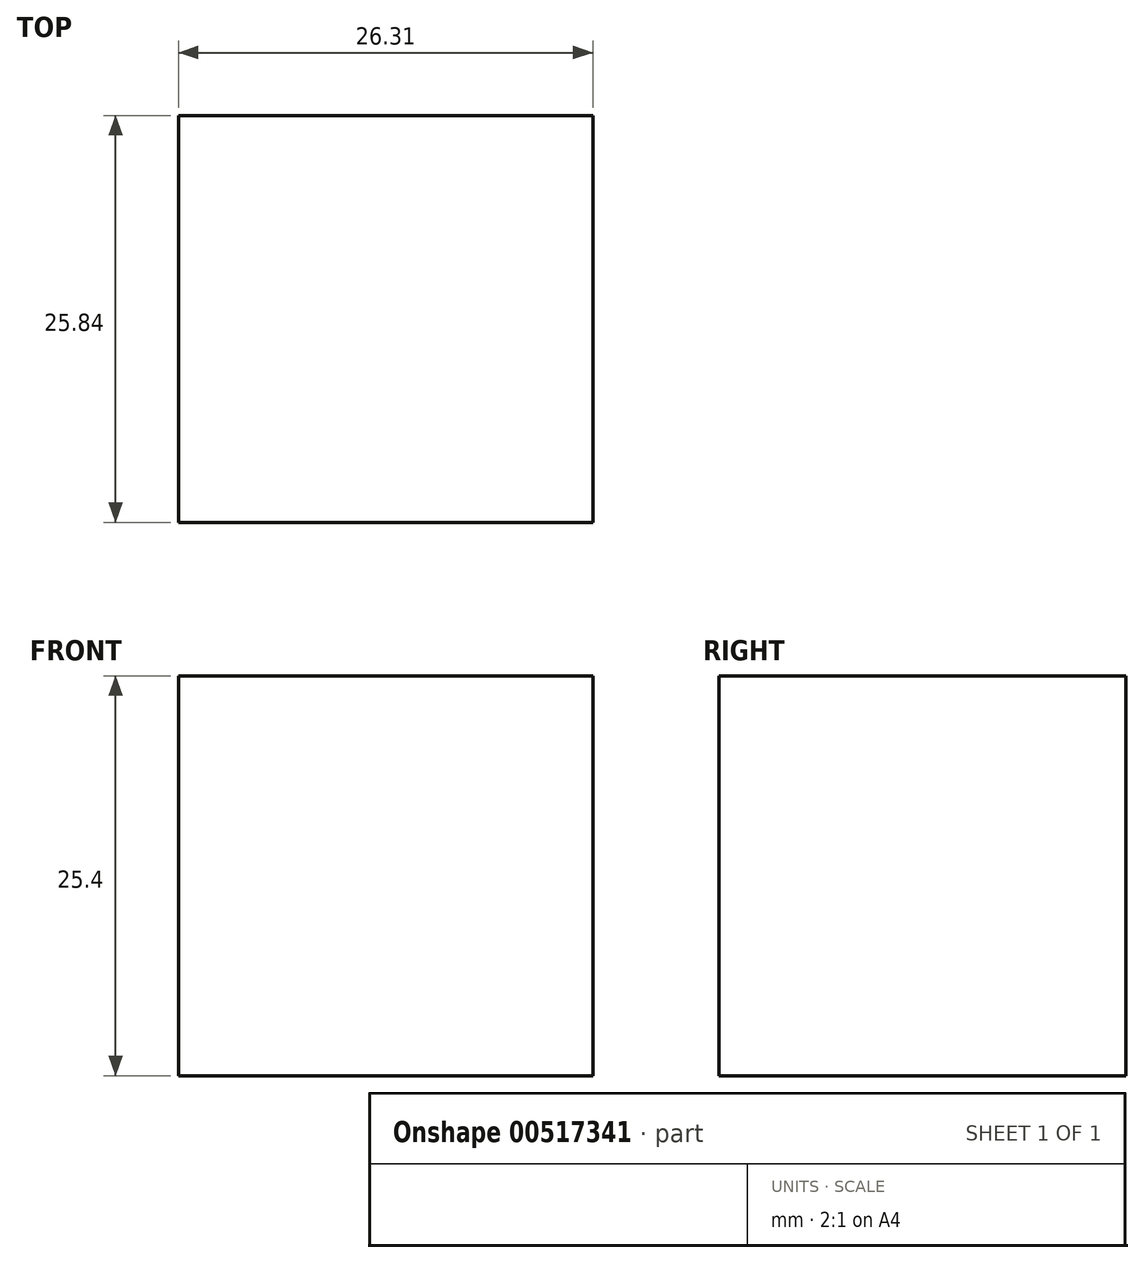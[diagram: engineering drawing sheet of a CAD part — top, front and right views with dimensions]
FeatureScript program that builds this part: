
annotation { "Feature Type Name" : "Feature", "Feature Type Description" : "" }
export const myFeature = defineFeature(function(context is Context, id is Id, definition is map)
    precondition{}
    {
        {
            var Q0;
            Q0=qCreatedBy(makeId("Top.planeOp"),FACE);
            var sketch = newSketch(context, id + "F0", { "sketchPlane" : qUnion([Q0])});
            skLineSegment(sketch, "E0", {"start": v(0, 0) * mm, "end": v(0, 25.84) * mm});
            skLineSegment(sketch, "E1", {"start": v(0, 25.84) * mm, "end": v(26.3, 25.84) * mm});
            skLineSegment(sketch, "E2", {"start": v(26.3, 25.84) * mm, "end": v(26.3, 0) * mm});
            skLineSegment(sketch, "E3", {"start": v(26.3, 0) * mm, "end": v(0, 0) * mm});
            skSolve(sketch);
        }
        {
            var Q0;
            Q0 = qSketchRegion(id + "F0", true);
            extrude(context, id + "F1", {"entities" : qUnion([Q0]), "depth" : 25.4 * mm, "offsetDistance" : 25.4 * mm});
        }
    });
